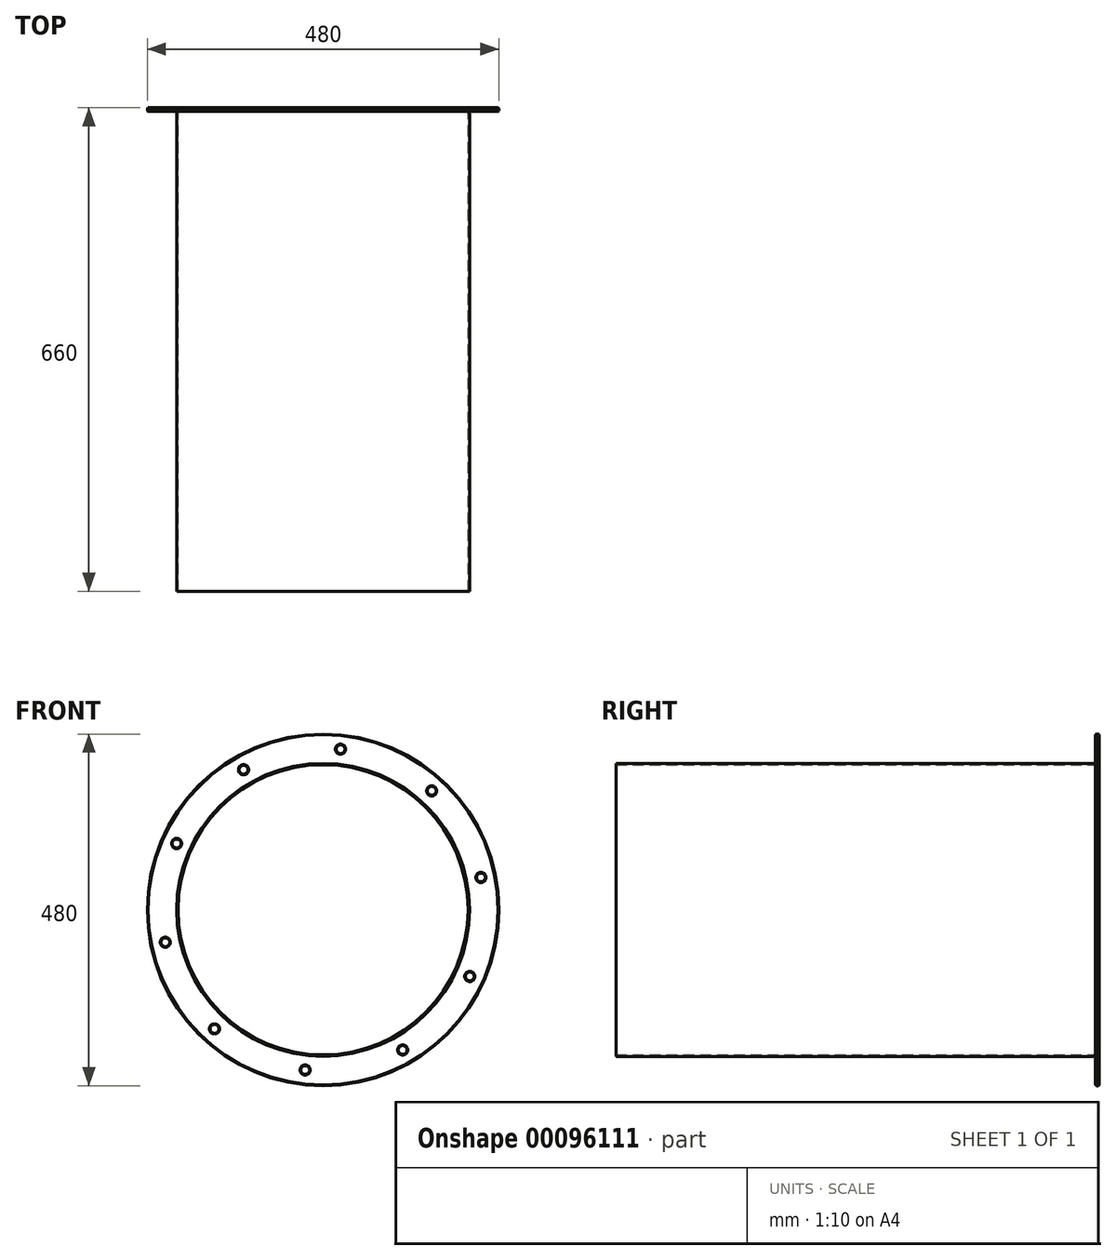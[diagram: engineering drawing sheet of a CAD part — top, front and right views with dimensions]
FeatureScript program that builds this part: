
annotation { "Feature Type Name" : "Feature", "Feature Type Description" : "" }
export const myFeature = defineFeature(function(context is Context, id is Id, definition is map)
    precondition{}
    {
        {
            var Q0;
            Q0=qCreatedBy(makeId("Front.planeOp"),FACE);
            var sketch = newSketch(context, id + "F0", { "sketchPlane" : qUnion([Q0])});
            skCircle(sketch, "E0", {"center": v(0, 0) * mm, "radius": 240 * mm});
            skCircle(sketch, "E1", {"center": v(0, 0) * mm, "radius": 200 * mm});
            skCircle(sketch, "E2", {"center": v(0, 0) * mm, "radius": 198 * mm});
            skCircle(sketch, "E3", {"center": v(200.35, -90.89) * mm, "radius": 6 * mm});
            skCircle(sketch, "E4", {"center": v(215.5, 44.23) * mm, "radius": 6 * mm});
            skCircle(sketch, "E5", {"center": v(148.35, 162.46) * mm, "radius": 6 * mm});
            skCircle(sketch, "E6", {"center": v(108.66, -191.3) * mm, "radius": 6 * mm});
            skCircle(sketch, "E7", {"center": v(-24.53, -218.63) * mm, "radius": 6 * mm});
            skCircle(sketch, "E8", {"center": v(-148.35, -162.46) * mm, "radius": 6 * mm});
            skCircle(sketch, "E9", {"center": v(-215.5, -44.23) * mm, "radius": 6 * mm});
            skCircle(sketch, "E10", {"center": v(-200.03, 90.54) * mm, "radius": 6 * mm});
            skCircle(sketch, "E11", {"center": v(-108.66, 191.3) * mm, "radius": 6 * mm});
            skCircle(sketch, "E12", {"center": v(23.82, 219.34) * mm, "radius": 6 * mm});
            skSolve(sketch);
        }
        {
            var Q0;
            Q0=makeQuery(id+"F0.imprint","IMPRINT",FACE,{"disambiguationData":[TD([[makeQuery(id+"F0.imprint","IMPRINT",EDGE,{"derivedFrom":sQuery(id+"F0.wireOp",EDGE,"E1")}),1.0]])]});
            extrude(context, id + "F1", {"entities" : qUnion([Q0]), "depth" : 655 * mm});
        }
        {
            var Q0;
            {var subQ0=sQuery(id+"F0.wireOp",EDGE,"adb980e5-db1f-4292-92ef-121c122598b0.5");Q0=makeQuery(id+"F0.imprint","IMPRINT",FACE,{"disambiguationData":[TD([[makeQuery(id+"F0.imprint","IMPRINT",EDGE,{"derivedFrom":subQ0}),1.0]])]});}
            var Q1;
            {var subQ0=sQuery(id+"F0.wireOp",EDGE,"adb980e5-db1f-4292-92ef-121c122598b0.6");Q1=makeQuery(id+"F0.imprint","IMPRINT",FACE,{"disambiguationData":[TD([[makeQuery(id+"F0.imprint","IMPRINT",EDGE,{"derivedFrom":subQ0}),1.0]])]});}
            var Q2;
            {var subQ0=sQuery(id+"F0.wireOp",EDGE,"adb980e5-db1f-4292-92ef-121c122598b0.8");Q2=makeQuery(id+"F0.imprint","IMPRINT",FACE,{"disambiguationData":[TD([[makeQuery(id+"F0.imprint","IMPRINT",EDGE,{"derivedFrom":subQ0}),1.0]])]});}
            var Q3;
            {var subQ0=sQuery(id+"F0.wireOp",EDGE,"adb980e5-db1f-4292-92ef-121c122598b0.4");Q3=makeQuery(id+"F0.imprint","IMPRINT",FACE,{"disambiguationData":[TD([[makeQuery(id+"F0.imprint","IMPRINT",EDGE,{"derivedFrom":subQ0}),1.0]])]});}
            var Q4;
            {var subQ0=sQuery(id+"F0.wireOp",EDGE,"adb980e5-db1f-4292-92ef-121c122598b0.3");Q4=makeQuery(id+"F0.imprint","IMPRINT",FACE,{"disambiguationData":[TD([[makeQuery(id+"F0.imprint","IMPRINT",EDGE,{"derivedFrom":subQ0}),1.0]])]});}
            var Q5;
            {var subQ0=sQuery(id+"F0.wireOp",EDGE,"adb980e5-db1f-4292-92ef-121c122598b0.2");Q5=makeQuery(id+"F0.imprint","IMPRINT",FACE,{"disambiguationData":[TD([[makeQuery(id+"F0.imprint","IMPRINT",EDGE,{"derivedFrom":subQ0}),1.0]])]});}
            var Q6;
            {var subQ0=sQuery(id+"F0.wireOp",EDGE,"adb980e5-db1f-4292-92ef-121c122598b0.1");Q6=makeQuery(id+"F0.imprint","IMPRINT",FACE,{"disambiguationData":[TD([[makeQuery(id+"F0.imprint","IMPRINT",EDGE,{"derivedFrom":subQ0}),1.0]])]});}
            var Q7;
            {var subQ0=sQuery(id+"F0.wireOp",EDGE,"adb980e5-db1f-4292-92ef-121c122598b0.0");Q7=makeQuery(id+"F0.imprint","IMPRINT",FACE,{"disambiguationData":[TD([[makeQuery(id+"F0.imprint","IMPRINT",EDGE,{"derivedFrom":subQ0}),1.0]])]});}
            var Q8;
            {var subQ0=sQuery(id+"F0.wireOp",EDGE,"adb980e5-db1f-4292-92ef-121c122598b0.7");Q8=makeQuery(id+"F0.imprint","IMPRINT",FACE,{"disambiguationData":[TD([[makeQuery(id+"F0.imprint","IMPRINT",EDGE,{"derivedFrom":subQ0}),1.0]])]});}
            var Q9;
            {var subQ0=sQuery(id+"F0.wireOp",EDGE,"adb980e5-db1f-4292-92ef-121c122598b0.2");Q9=makeQuery(id+"F0.imprint","IMPRINT",FACE,{"disambiguationData":[TD([[makeQuery(id+"F0.imprint","IMPRINT",EDGE,{"derivedFrom":subQ0}),1.0]])]});}
            var Q10;
            {var subQ0=sQuery(id+"F0.wireOp",EDGE,"adb980e5-db1f-4292-92ef-121c122598b0.9");Q10=makeQuery(id+"F0.imprint","IMPRINT",FACE,{"disambiguationData":[TD([[makeQuery(id+"F0.imprint","IMPRINT",EDGE,{"derivedFrom":subQ0}),1.0]])]});}
            var Q11;
            Q11=makeQuery(id+"F0.imprint","IMPRINT",FACE,{"disambiguationData":[TD([[makeQuery(id+"F0.imprint","IMPRINT",EDGE,{"derivedFrom":sQuery(id+"F0.wireOp",EDGE,"E0")}),1.0]])]});
            var Q12;
            Q12=makeQuery(id+"F0.imprint","IMPRINT",FACE,{"disambiguationData":[TD([[makeQuery(id+"F0.imprint","IMPRINT",EDGE,{"derivedFrom":sQuery(id+"F0.wireOp",EDGE,"E1")}),1.0]])]});
            var Q13;
            Q13=makeQuery(id+"F0.imprint","IMPRINT",FACE,{"disambiguationData":[TD([[makeQuery(id+"F0.imprint","IMPRINT",EDGE,{"derivedFrom":sQuery(id+"F0.wireOp",EDGE,"E1")}),-1.0]])]});
            extrude(context, id + "F2", {"entities" : qUnion([Q0, Q1, Q2, Q3, Q4, Q5, Q6, Q7, Q8, Q9, Q10, Q11, Q12, Q13]), "oppositeDirection" : true, "depth" : 5 * mm});
        }
        {
            var Q0;
            Q0=makeQuery(id+"F2.opExtrude","CAP_EDGE",EDGE,{"disambiguationData":[OSD([sQuery(id+"F0.wireOp",EDGE,"E2")])],"isStart":false});
            fillet(context, id + "F3", {"entities" : qUnion([Q0]), "radius" : 5 * mm, "tangentPropagation" : true, "allowEdgeOverflow" : false});
        }
        {
            var Q0;
            Q0=makeQuery(id+"F1.opExtrude","CAP_EDGE",EDGE,{"disambiguationData":[OSD([sQuery(id+"F0.wireOp",EDGE,"E1")])],"isStart":true});
            fillet(context, id + "F4", {"entities" : qUnion([Q0]), "radius" : 5 * mm, "tangentPropagation" : true, "allowEdgeOverflow" : false});
        }
        {
            var Q0;
            Q0=makeQuery(id+"F2.opExtrude","CAP_FACE",FACE,{"disambiguationData":[OSD([sQuery(id+"F0.wireOp",EDGE,"E0"),sQuery(id+"F0.wireOp",EDGE,"E2"),sQuery(id+"F0.wireOp",EDGE,"E3"),sQuery(id+"F0.wireOp",EDGE,"E4"),sQuery(id+"F0.wireOp",EDGE,"E5"),sQuery(id+"F0.wireOp",EDGE,"E6"),sQuery(id+"F0.wireOp",EDGE,"E7"),sQuery(id+"F0.wireOp",EDGE,"E8"),sQuery(id+"F0.wireOp",EDGE,"E9"),sQuery(id+"F0.wireOp",EDGE,"E10"),sQuery(id+"F0.wireOp",EDGE,"E11"),sQuery(id+"F0.wireOp",EDGE,"E12")])],"isStart":true});
            chamfer(context, id + "F5", {"entities" : qUnion([Q0]), "width" : 1 * mm, "tangentPropagation" : true});
        }
        {
            var Q0;
            Q0=makeQuery(id+"F2.opExtrude","CAP_FACE",FACE,{"disambiguationData":[OSD([sQuery(id+"F0.wireOp",EDGE,"E0"),sQuery(id+"F0.wireOp",EDGE,"E2"),sQuery(id+"F0.wireOp",EDGE,"E3"),sQuery(id+"F0.wireOp",EDGE,"E4"),sQuery(id+"F0.wireOp",EDGE,"E5"),sQuery(id+"F0.wireOp",EDGE,"E6"),sQuery(id+"F0.wireOp",EDGE,"E7"),sQuery(id+"F0.wireOp",EDGE,"E8"),sQuery(id+"F0.wireOp",EDGE,"E9"),sQuery(id+"F0.wireOp",EDGE,"E10"),sQuery(id+"F0.wireOp",EDGE,"E11"),sQuery(id+"F0.wireOp",EDGE,"E12")])],"isStart":false});
            chamfer(context, id + "F6", {"entities" : qUnion([Q0]), "width" : 1 * mm, "tangentPropagation" : true});
        }
        {
            var Q0;
            Q0=qCreatedBy(makeId("Top.planeOp"),FACE);
            var sketch = newSketch(context, id + "F7", { "sketchPlane" : qUnion([Q0])});
            skCircle(sketch, "E13", {"center": v(0, -178.16) * mm, "radius": 150 * mm});
            skSolve(sketch);
        }
        {
            var Q0;
            Q0=sQuery(id+"F7.wireOp",VERTEX,"E13.center");
            var Q1;
            Q1=makeQuery(id+"F2.opExtrude","SWEPT_BODY",BODY,{"disambiguationData":[OSD([sQuery(id+"F0.wireOp",EDGE,"E0"),sQuery(id+"F0.wireOp",EDGE,"E2"),sQuery(id+"F0.wireOp",EDGE,"E3"),sQuery(id+"F0.wireOp",EDGE,"E4"),sQuery(id+"F0.wireOp",EDGE,"E5"),sQuery(id+"F0.wireOp",EDGE,"E6"),sQuery(id+"F0.wireOp",EDGE,"E7"),sQuery(id+"F0.wireOp",EDGE,"E8"),sQuery(id+"F0.wireOp",EDGE,"E9"),sQuery(id+"F0.wireOp",EDGE,"E10"),sQuery(id+"F0.wireOp",EDGE,"E11"),sQuery(id+"F0.wireOp",EDGE,"E12")])]});
            hole(context, id + "F8", {"style" : HoleStyle.SIMPLE, "endStyle" : HoleEndStyle.THROUGH, "oppositeDirection" : true, "holeDiameter" : 300 * mm, "locations" : qUnion([Q0]), "scope" : qUnion([Q1]), "isTappedThrough" : true});
        }
    });
